# Revit family: Zenit Heco E W 400-950 Р19
name_source: partatom
category: Оборудование
units: mm (PartAtom-declared; Revit-internal decimal feet)

## family parameters
Всегда вертикально = Да
Классификация = Нет
На основе рабочей плоскости = Нет
Общий = Нет
При загрузке вырезать с полостями = Нет
Размер круглого соединителя = Использовать диаметр
Тип детали = Нормальный
Точка расчета площади = Нет

## types (7) — shared parameters
ADSK_Единица измерения = шт.
ADSK_Завод-изготовитель = ООО «Турков»
ADSK_Количество = 1
ADSK_Количество фаз = 1
ADSK_Наименование = Приточно-вытяжная установка с рекуперацией и нагревателем Zenit HECO в стальном корпусе
ADSK_Напряжение = 220 В
ВВ высота = 40 мм
ВВ меду осями = 370 мм
Д1 к от края = 50 мм
Д1 между кр и к = 3 мм
Защелка У = 13 мм
Защелка Х1 = 180 мм
Защелка Х2 = 30 мм
Защелка2 = Да
КА высота = 100 мм
КА длина = 245 мм
КА от края = 160 мм
КА ширина = 190 мм
СЗ КА = 200 мм
СЗ Ф = 200 мм
СУ подкл = 13 мм
Ширина дверцы1 = 325 мм

## per-type parameters (varying)
| type | A ширина | ADSK_Масса | ADSK_Номинальная мощность | ADSK_Расход воздуха | ADSK_Свободный напор воздуха | ADSK_Ток | B высота | C толщина | Dn | ВВ от края | ВП X | ВП Y | Вод подогр | Смесит узел | Ширина дверцы2 | Эл подогр | угол |
| Zenit Heco XM 360 1,5E220 | 1340 мм | 70 | 1820 Вт | 400.0 м³/ч | 388.0 Па | 8 А | 750 мм | 406 мм | 160 мм | 170 мм | 495 мм | 85 мм | Нет | Петли большие | 325 мм | Да | 26.57° |
| Zenit Heco XM 560 1,5/3E220 | 1340 мм | 85 | 1830 Вт | 600.0 м³/ч | 163.0 Па | 8 А | 750 мм | 506 мм | 200 мм | 170 мм | 495 мм | 85 мм | Нет | Петли большие | 210 мм | Да | 21.80° |
| Zenit Heco XM 760 W220 | 1340 мм | 105 | 711 Вт | 800.0 м³/ч | 342.0 Па | 3 А | 750 мм | 606 мм | 250 мм | 189 мм | 108 мм | 105 мм | Да | Смесительный узел парал : 800 | 210 мм | Нет | 17.74° |
| Zenit Heco XM 910 3/4,5E220 | 1340 мм | 125 | 3640 Вт | 950.0 м³/ч | 285.0 Па | 17 А | 750 мм | 710 мм | 250 мм | 189 мм | 495 мм | 85 мм | Нет | Петли большие | 210 мм | Да | 17.74° |
| Zenit Heco XM 560 W220 | 1340 мм | 85 | 400 Вт | 600.0 м³/ч | 163.0 Па | 2 А | 750 мм | 506 мм | 200 мм | 170 мм | 118 мм | 100 мм | Да | Смесительный узел парал : 600 | 210 мм | Нет | 21.80° |
| Zenit Heco XM 910 W220 | 1340 мм | 125 | 711 Вт | 950.0 м³/ч | 285.0 Па | 3 А | 750 мм | 710 мм | 250 мм | 189 мм | 108 мм | 157 мм | Да | Смесительный узел парал : 800 | 210 мм | Нет | 17.74° |
| Zenit Heco XM 760 3/4,5E220 | 1346 мм | 125 | 0 Вт | 760.0 м³/ч | 285.0 Па | 0 А | 756 мм | 610 мм | 250 мм | 189 мм | 108 мм | 157 мм | Нет | Смесительный узел парал : 800 | 210 мм | Да | 17.74° |

note: column(s) folded — value = type name in every type: ADSK_Марка

## geometry (parser evidence)
native form markers: Sweep x4
no freeform markers — native parametric forms only
